# Revit family: ledwaterproof-b_l1450-50w-6500_543022018000
name_source: partatom
category: Leuchten
revit_build: Autodesk Revit 2016 (Build: 20190508_0715(x64)
units: mm (PartAtom-declared; Revit-internal decimal feet)

## family parameters
Basisbauteil = Fläche
Beim Laden mit Abzugskörper schneiden = Nein
Bemaßung runder Anschluss = Durchmesser verwenden
Gemeinsam genutzt = Nein
Lichtquelle = Nein
Raumberechnungspunkt = Nein
Teiletyp = Normal

## types (1)
- LEDWaterproof-B L1450-50W-6500 (1 x LED, 6250 lm)
    Approval mark = CE
    Beschreibung = Cost effective ''sealed-for-life'' waterproof luminaire. High efficacy of 125 lm/w. Up to 60% lower energy consumption compared to traditional TL lighting. Quick installation through the easy to open endcap. Supplied with stainless steel ceiling and suspension clips.
    CIE Flux Codes = 44 73 91 94 100
    Control Gear = Electronic ballast
    Height = 69 mm
    Hersteller = OPPLE
    Lamp Light Flux = 6250 lm
    Lamp count = 1
    Lampe = 1 x LED
    Length = 70 mm
    Luminous efficacy = 125 lm/W
    ModVariant = Nein
    Modell = 543022018000
    Mounting Place = Ceiling
    Mounting Type = Surface mounted
    Number of Poles = 1
    OnlyDefault = Ja
    Power Factor = 1
    Product Name = LEDWaterproof-B L1450-50W-6500
    Product group = Waterproof Basic
    ProductGroupID = 345
    Protection Class = Protection class II
    Protection Degree = IP 65
    RLX_Detail_Level = 1
    RlxData = <blob elided: 27253 chars, md5=ebc52ac2>
    Scheinlast = 50 VA
    Socket = socket
    Standby Power = 0 W
    System Light Flux = 6250 lm
    System Power = 50 W
    Typenbild = product20waterproof20basic.jpg
    Typenkommentare = Product without accessories
    URL = http://relux.com
    VarID = ---
    Voltage = 0 V
    Vorgabe-Ansicht = 1800 mm
    Weight = 0.00 kg
    Width = 1488 mm

## geometry (parser evidence)
native form markers: Blend x4, Sweep x15
no freeform markers — native parametric forms only
